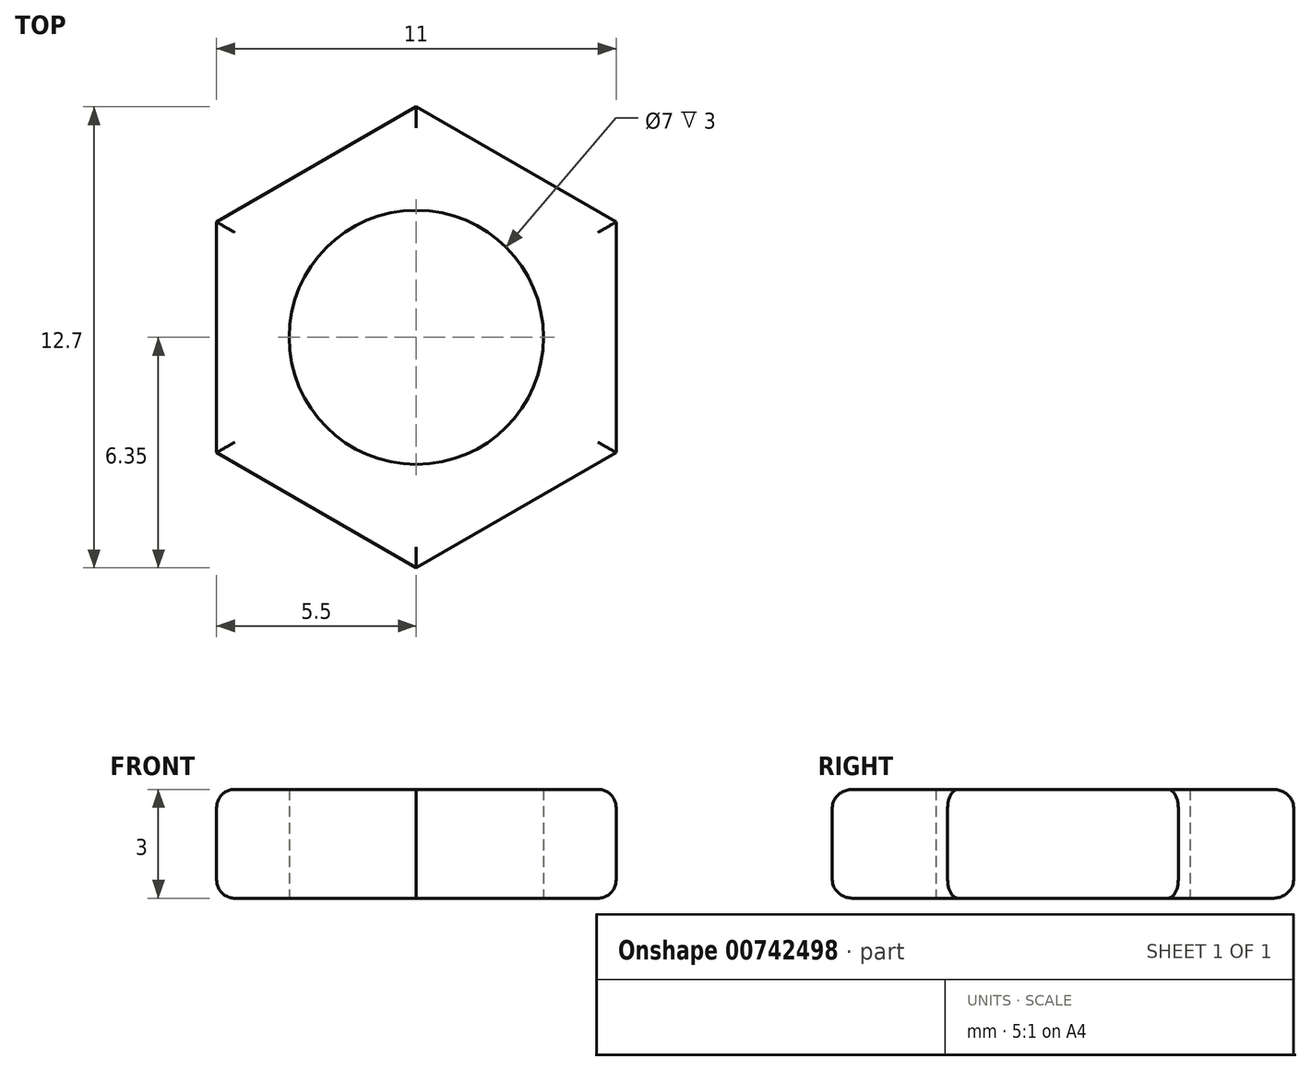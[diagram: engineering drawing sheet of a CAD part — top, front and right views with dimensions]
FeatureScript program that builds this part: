
annotation { "Feature Type Name" : "Feature", "Feature Type Description" : "" }
export const myFeature = defineFeature(function(context is Context, id is Id, definition is map)
    precondition{}
    {
        {
            var Q0;
            Q0=qCreatedBy(makeId("Top.planeOp"),FACE);
            var sketch = newSketch(context, id + "F0", { "sketchPlane" : qUnion([Q0])});
            skCircle(sketch, "E0.cCircle", {"center": v(0, 0) * mm, "radius": 5.5 * mm, "construction": true});
            skLineSegment(sketch, "E0.0", {"start": v(5.5, 3.18) * mm, "end": v(5.5, -3.18) * mm});
            skLineSegment(sketch, "E0.1", {"start": v(5.5, -3.18) * mm, "end": v(0, -6.35) * mm});
            skLineSegment(sketch, "E0.2", {"start": v(0, -6.35) * mm, "end": v(-5.5, -3.18) * mm});
            skLineSegment(sketch, "E0.3", {"start": v(-5.5, -3.18) * mm, "end": v(-5.5, 3.18) * mm});
            skLineSegment(sketch, "E0.4", {"start": v(-5.5, 3.18) * mm, "end": v(0, 6.35) * mm});
            skLineSegment(sketch, "E0.5", {"start": v(0, 6.35) * mm, "end": v(5.5, 3.18) * mm});
            skPoint(sketch, "E0.0.midPoint", {"position": v(5.5, 0) * mm});
            skCircle(sketch, "E1", {"center": v(0, 0) * mm, "radius": 3.5 * mm});
            skSolve(sketch);
        }
        {
            var Q0;
            Q0=makeQuery(id+"F0.imprint","IMPRINT",FACE,{"disambiguationData":[TD([[makeQuery(id+"F0.imprint","IMPRINT",EDGE,{"derivedFrom":sQuery(id+"F0.wireOp",EDGE,"E0.0")}),-1.0]])]});
            extrude(context, id + "F1", {"entities" : qUnion([Q0]), "depth" : 3 * mm, "offsetDistance" : 25 * mm});
        }
        {
            var Q0;
            Q0=makeQuery(id+"F1.opExtrude","CAP_EDGE",EDGE,{"disambiguationData":[OSD([sQuery(id+"F0.wireOp",EDGE,"E0.1")])],"isStart":false});
            var Q1;
            Q1=makeQuery(id+"F1.opExtrude","CAP_EDGE",EDGE,{"disambiguationData":[OSD([sQuery(id+"F0.wireOp",EDGE,"E0.2")])],"isStart":false});
            var Q2;
            Q2=makeQuery(id+"F1.opExtrude","CAP_EDGE",EDGE,{"disambiguationData":[OSD([sQuery(id+"F0.wireOp",EDGE,"E0.4")])],"isStart":false});
            var Q3;
            Q3=makeQuery(id+"F1.opExtrude","CAP_EDGE",EDGE,{"disambiguationData":[OSD([sQuery(id+"F0.wireOp",EDGE,"E0.3")])],"isStart":false});
            var Q4;
            Q4=makeQuery(id+"F1.opExtrude","CAP_EDGE",EDGE,{"disambiguationData":[OSD([sQuery(id+"F0.wireOp",EDGE,"E0.0")])],"isStart":false});
            var Q5;
            Q5=makeQuery(id+"F1.opExtrude","CAP_EDGE",EDGE,{"disambiguationData":[OSD([sQuery(id+"F0.wireOp",EDGE,"E0.5")])],"isStart":false});
            fillet(context, id + "F2", {"entities" : qUnion([Q0, Q1, Q2, Q3, Q4, Q5]), "radius" : 0.5 * mm, "allowEdgeOverflow" : false});
        }
        {
            var Q0;
            Q0=makeQuery(id+"F1.opExtrude","CAP_EDGE",EDGE,{"disambiguationData":[OSD([sQuery(id+"F0.wireOp",EDGE,"E0.1")])],"isStart":true});
            var Q1;
            Q1=makeQuery(id+"F1.opExtrude","CAP_EDGE",EDGE,{"disambiguationData":[OSD([sQuery(id+"F0.wireOp",EDGE,"E0.2")])],"isStart":true});
            var Q2;
            Q2=makeQuery(id+"F1.opExtrude","CAP_EDGE",EDGE,{"disambiguationData":[OSD([sQuery(id+"F0.wireOp",EDGE,"E0.4")])],"isStart":true});
            var Q3;
            Q3=makeQuery(id+"F1.opExtrude","CAP_EDGE",EDGE,{"disambiguationData":[OSD([sQuery(id+"F0.wireOp",EDGE,"E0.3")])],"isStart":true});
            var Q4;
            Q4=makeQuery(id+"F1.opExtrude","CAP_EDGE",EDGE,{"disambiguationData":[OSD([sQuery(id+"F0.wireOp",EDGE,"E0.5")])],"isStart":true});
            var Q5;
            Q5=makeQuery(id+"F1.opExtrude","CAP_EDGE",EDGE,{"disambiguationData":[OSD([sQuery(id+"F0.wireOp",EDGE,"E0.0")])],"isStart":true});
            fillet(context, id + "F3", {"entities" : qUnion([Q0, Q1, Q2, Q3, Q4, Q5]), "radius" : 0.5 * mm, "tangentPropagation" : true, "allowEdgeOverflow" : false});
        }
    });
